# Revit family: RN 80022 Optipress-Aquaplus-Schiebemuffe
name_source: partatom
category: Rohrformteile
units: mm (PartAtom-declared; Revit-internal decimal feet)

## family parameters
Arbeitsebenenbasiert = Nein
Beim Laden mit Abzugskörper schneiden = Nein
Bemaßung runder Anschluss = Durchmesser verwenden
Gemeinsam genutzt = Nein
Immer vertikal = Ja
Teiletyp = Verbindung

## types (11) — shared parameters
1.010.00.2 Blattnummer der Richtlinie = 29
1.010.00.3 Ausgabedatum (Monat) der Richtlinie = 201308
1.010.00.4 Herstellername = R. Nussbaum AG
1.010.00.5 Revisionsdatum der Datei = 20190521
1.010.00.6 Webadresse des Herstellers = http://www.nussbaum.ch
1.100.00.4 Produktbezeichnung = Versorgung
1.110.00.2 Index = 4
1.110.00.4 Produktbezeichnung = Optipress
1.960/3L.00.8 Link (URL) = https://www.nussbaum.ch
29.700.00.4 Produktname = Optipress-Aquaplus-Schiebemuffe
29.700.00.5 Produktkennung = 2
29.700.00.6 Querschnittsform = 1
29.700.00.7 Nennweitensystem = DN
29.700.00.8 Nenndrucksystem = PN
29.710.02.4 Nenndruck = 16
29.710.02.5 max. zul. Überdruck [hPa] = 1600
29.710.02.7 max. zul. Dauer-Betriebsdruck [hPa] = 1600
29.710.02.9 max. zul. Dauer-Betriebstemperatur [°C] = 95
Connector Visibility = Nein
EnclosingSpace Visibility = Nein

## per-type parameters (varying)
- 80022.22, Optipress-Aquaplus-Schiebemuffe, DN=12, L=80: 1.800.00.3 TGA-Nummer=01900400000000000000000000000000000000000000000016000000000000000001; 1.810.00.3 Hersteller-Bestellnummer=80022.22; 1.810.00.4 DATANORM-Nummer=80022.22; 1.810.00.5 StLB-Nummer=265.212; 1.810.00.6 GTIN-Nummer=7612945051301; 29.710.02.10 Formstück-Gewicht [kg]=0.051; 29.710.02.3 Benennung=Optipress-Aquaplus-Schiebemuffe, DN=12, L=80; CONNECTOR0_DIAMETER_dX_0r=12 mm  [stored 0.0393701 ft]; CONNECTOR0_dX_01=22 mm; CONNECTOR0_ref_dX=22 mm; CONNECTOR1_DIAMETER_dX_0r=12 mm  [stored 0.0393701 ft]; CONNECTOR1_dX_00=59 mm; CONNECTOR1_dX_01=81 mm; CONNECTOR1_ref_dX=59 mm; R. Nussbaum AG 80022.22 de Visibility=Ja; R. Nussbaum AG 80022.23 de Visibility=Nein; R. Nussbaum AG 80022.24 de Visibility=Nein; R. Nussbaum AG 80022.25 de Visibility=Nein; R. Nussbaum AG 80022.26 de Visibility=Nein; R. Nussbaum AG 80022.27 de Visibility=Nein; R. Nussbaum AG 80022.28 de Visibility=Nein; R. Nussbaum AG 80022.70 de Visibility=Nein; R. Nussbaum AG 80022.71 de Visibility=Nein; R. Nussbaum AG 80022.72 de Visibility=Nein; R. Nussbaum AG 80022.73 de Visibility=Nein
- 80022.23, Optipress-Aquaplus-Schiebemuffe, DN=15, L=80: 1.800.00.3 TGA-Nummer=01900400000000000000000000000000000000000000000016000000000000000002; 1.810.00.3 Hersteller-Bestellnummer=80022.23; 1.810.00.4 DATANORM-Nummer=80022.23; 1.810.00.5 StLB-Nummer=265.213; 1.810.00.6 GTIN-Nummer=7612945051318; 29.710.02.10 Formstück-Gewicht [kg]=0.063; 29.710.02.3 Benennung=Optipress-Aquaplus-Schiebemuffe, DN=15, L=80; CONNECTOR0_DIAMETER_dX_0r=15 mm; CONNECTOR0_dX_01=22 mm; CONNECTOR0_ref_dX=22 mm; CONNECTOR1_DIAMETER_dX_0r=15 mm; CONNECTOR1_dX_00=59 mm; CONNECTOR1_dX_01=81 mm; CONNECTOR1_ref_dX=59 mm; R. Nussbaum AG 80022.22 de Visibility=Nein; R. Nussbaum AG 80022.23 de Visibility=Ja; R. Nussbaum AG 80022.24 de Visibility=Nein; R. Nussbaum AG 80022.25 de Visibility=Nein; R. Nussbaum AG 80022.26 de Visibility=Nein; R. Nussbaum AG 80022.27 de Visibility=Nein; R. Nussbaum AG 80022.28 de Visibility=Nein; R. Nussbaum AG 80022.70 de Visibility=Nein; R. Nussbaum AG 80022.71 de Visibility=Nein; R. Nussbaum AG 80022.72 de Visibility=Nein; R. Nussbaum AG 80022.73 de Visibility=Nein
- 80022.24, Optipress-Aquaplus-Schiebemuffe, DN=20, L=80: 1.800.00.3 TGA-Nummer=01900400000000000000000000000000000000000000000016000000000000000003; 1.810.00.3 Hersteller-Bestellnummer=80022.24; 1.810.00.4 DATANORM-Nummer=80022.24; 1.810.00.5 StLB-Nummer=265.214; 1.810.00.6 GTIN-Nummer=7612945051325; 29.710.02.10 Formstück-Gewicht [kg]=0.082; 29.710.02.3 Benennung=Optipress-Aquaplus-Schiebemuffe, DN=20, L=80; CONNECTOR0_DIAMETER_dX_0r=20 mm; CONNECTOR0_dX_01=24 mm; CONNECTOR0_ref_dX=24 mm; CONNECTOR1_DIAMETER_dX_0r=20 mm; CONNECTOR1_dX_00=57 mm; CONNECTOR1_dX_01=81 mm; CONNECTOR1_ref_dX=57 mm; R. Nussbaum AG 80022.22 de Visibility=Nein; R. Nussbaum AG 80022.23 de Visibility=Nein; R. Nussbaum AG 80022.24 de Visibility=Ja; R. Nussbaum AG 80022.25 de Visibility=Nein; R. Nussbaum AG 80022.26 de Visibility=Nein; R. Nussbaum AG 80022.27 de Visibility=Nein; R. Nussbaum AG 80022.28 de Visibility=Nein; R. Nussbaum AG 80022.70 de Visibility=Nein; R. Nussbaum AG 80022.71 de Visibility=Nein; R. Nussbaum AG 80022.72 de Visibility=Nein; R. Nussbaum AG 80022.73 de Visibility=Nein
- 80022.25, Optipress-Aquaplus-Schiebemuffe, DN=25, L=95: 1.800.00.3 TGA-Nummer=01900400000000000000000000000000000000000000000016000000000000000004; 1.810.00.3 Hersteller-Bestellnummer=80022.25; 1.810.00.4 DATANORM-Nummer=80022.25; 1.810.00.5 StLB-Nummer=265.215; 1.810.00.6 GTIN-Nummer=7612945051332; 29.710.02.10 Formstück-Gewicht [kg]=0.119; 29.710.02.3 Benennung=Optipress-Aquaplus-Schiebemuffe, DN=25, L=95; CONNECTOR0_DIAMETER_dX_0r=25 mm  [stored 0.082021 ft]; CONNECTOR0_dX_01=24 mm; CONNECTOR0_ref_dX=24 mm; CONNECTOR1_DIAMETER_dX_0r=25 mm  [stored 0.082021 ft]; CONNECTOR1_dX_00=72 mm; CONNECTOR1_dX_01=96 mm; CONNECTOR1_ref_dX=72 mm; R. Nussbaum AG 80022.22 de Visibility=Nein; R. Nussbaum AG 80022.23 de Visibility=Nein; R. Nussbaum AG 80022.24 de Visibility=Nein; R. Nussbaum AG 80022.25 de Visibility=Ja; R. Nussbaum AG 80022.26 de Visibility=Nein; R. Nussbaum AG 80022.27 de Visibility=Nein; R. Nussbaum AG 80022.28 de Visibility=Nein; R. Nussbaum AG 80022.70 de Visibility=Nein; R. Nussbaum AG 80022.71 de Visibility=Nein; R. Nussbaum AG 80022.72 de Visibility=Nein; R. Nussbaum AG 80022.73 de Visibility=Nein
- 80022.26, Optipress-Aquaplus-Schiebemuffe, DN=32, L=105: 1.800.00.3 TGA-Nummer=01900400000000000000000000000000000000000000000016000000000000000005; 1.810.00.3 Hersteller-Bestellnummer=80022.26; 1.810.00.4 DATANORM-Nummer=80022.26; 1.810.00.5 StLB-Nummer=265.216; 1.810.00.6 GTIN-Nummer=7612945051349; 29.710.02.10 Formstück-Gewicht [kg]=0.16; 29.710.02.3 Benennung=Optipress-Aquaplus-Schiebemuffe, DN=32, L=105; CONNECTOR0_DIAMETER_dX_0r=32 mm  [stored 0.104987 ft]; CONNECTOR0_dX_01=26 mm  [stored 0.0853018 ft]; CONNECTOR0_ref_dX=26 mm  [stored 0.0853018 ft]; CONNECTOR1_DIAMETER_dX_0r=32 mm  [stored 0.104987 ft]; CONNECTOR1_dX_00=80 mm; CONNECTOR1_dX_01=106 mm; CONNECTOR1_ref_dX=80 mm; R. Nussbaum AG 80022.22 de Visibility=Nein; R. Nussbaum AG 80022.23 de Visibility=Nein; R. Nussbaum AG 80022.24 de Visibility=Nein; R. Nussbaum AG 80022.25 de Visibility=Nein; R. Nussbaum AG 80022.26 de Visibility=Ja; R. Nussbaum AG 80022.27 de Visibility=Nein; R. Nussbaum AG 80022.28 de Visibility=Nein; R. Nussbaum AG 80022.70 de Visibility=Nein; R. Nussbaum AG 80022.71 de Visibility=Nein; R. Nussbaum AG 80022.72 de Visibility=Nein; R. Nussbaum AG 80022.73 de Visibility=Nein
- 80022.27, Optipress-Aquaplus-Schiebemuffe, DN=40, L=120: 1.800.00.3 TGA-Nummer=01900400000000000000000000000000000000000000000016000000000000000006; 1.810.00.3 Hersteller-Bestellnummer=80022.27; 1.810.00.4 DATANORM-Nummer=80022.27; 1.810.00.5 StLB-Nummer=265.217; 1.810.00.6 GTIN-Nummer=7612945051356; 29.710.02.10 Formstück-Gewicht [kg]=0.271; 29.710.02.3 Benennung=Optipress-Aquaplus-Schiebemuffe, DN=40, L=120; CONNECTOR0_DIAMETER_dX_0r=40 mm; CONNECTOR0_dX_01=36 mm; CONNECTOR0_ref_dX=36 mm; CONNECTOR1_DIAMETER_dX_0r=40 mm; CONNECTOR1_dX_00=85 mm; CONNECTOR1_dX_01=121 mm; CONNECTOR1_ref_dX=85 mm; R. Nussbaum AG 80022.22 de Visibility=Nein; R. Nussbaum AG 80022.23 de Visibility=Nein; R. Nussbaum AG 80022.24 de Visibility=Nein; R. Nussbaum AG 80022.25 de Visibility=Nein; R. Nussbaum AG 80022.26 de Visibility=Nein; R. Nussbaum AG 80022.27 de Visibility=Ja; R. Nussbaum AG 80022.28 de Visibility=Nein; R. Nussbaum AG 80022.70 de Visibility=Nein; R. Nussbaum AG 80022.71 de Visibility=Nein; R. Nussbaum AG 80022.72 de Visibility=Nein; R. Nussbaum AG 80022.73 de Visibility=Nein
- 80022.28, Optipress-Aquaplus-Schiebemuffe, DN=50, L=136: 1.800.00.3 TGA-Nummer=01900400000000000000000000000000000000000000000016000000000000000007; 1.810.00.3 Hersteller-Bestellnummer=80022.28; 1.810.00.4 DATANORM-Nummer=80022.28; 1.810.00.5 StLB-Nummer=265.218; 1.810.00.6 GTIN-Nummer=7612945051363; 29.710.02.10 Formstück-Gewicht [kg]=0.335; 29.710.02.3 Benennung=Optipress-Aquaplus-Schiebemuffe, DN=50, L=136; CONNECTOR0_DIAMETER_dX_0r=50 mm; CONNECTOR0_dX_01=40 mm; CONNECTOR0_ref_dX=40 mm; CONNECTOR1_DIAMETER_dX_0r=50 mm; CONNECTOR1_dX_00=96 mm; CONNECTOR1_dX_01=136 mm; CONNECTOR1_ref_dX=96 mm; R. Nussbaum AG 80022.22 de Visibility=Nein; R. Nussbaum AG 80022.23 de Visibility=Nein; R. Nussbaum AG 80022.24 de Visibility=Nein; R. Nussbaum AG 80022.25 de Visibility=Nein; R. Nussbaum AG 80022.26 de Visibility=Nein; R. Nussbaum AG 80022.27 de Visibility=Nein; R. Nussbaum AG 80022.28 de Visibility=Ja; R. Nussbaum AG 80022.70 de Visibility=Nein; R. Nussbaum AG 80022.71 de Visibility=Nein; R. Nussbaum AG 80022.72 de Visibility=Nein; R. Nussbaum AG 80022.73 de Visibility=Nein
- 80022.71, Optipress-Aquaplus-Schiebemuffe, DN=65, L=125: 1.800.00.3 TGA-Nummer=01900400000000000000000000000000000000000000000016000000000000000008; 1.810.00.3 Hersteller-Bestellnummer=80022.71; 1.810.00.4 DATANORM-Nummer=80022.71; 1.810.00.5 StLB-Nummer=265.221; 1.810.00.6 GTIN-Nummer=7612945655318; 29.710.02.10 Formstück-Gewicht [kg]=0.587; 29.710.02.3 Benennung=Optipress-Aquaplus-Schiebemuffe, DN=65, L=125; CONNECTOR0_DIAMETER_dX_0r=65 mm; CONNECTOR0_dX_01=50 mm; CONNECTOR0_ref_dX=50 mm; CONNECTOR1_DIAMETER_dX_0r=65 mm; CONNECTOR1_dX_00=75 mm; CONNECTOR1_dX_01=125 mm; CONNECTOR1_ref_dX=75 mm; R. Nussbaum AG 80022.22 de Visibility=Nein; R. Nussbaum AG 80022.23 de Visibility=Nein; R. Nussbaum AG 80022.24 de Visibility=Nein; R. Nussbaum AG 80022.25 de Visibility=Nein; R. Nussbaum AG 80022.26 de Visibility=Nein; R. Nussbaum AG 80022.27 de Visibility=Nein; R. Nussbaum AG 80022.28 de Visibility=Nein; R. Nussbaum AG 80022.70 de Visibility=Nein; R. Nussbaum AG 80022.71 de Visibility=Ja; R. Nussbaum AG 80022.72 de Visibility=Nein; R. Nussbaum AG 80022.73 de Visibility=Nein
- 80022.72, Optipress-Aquaplus-Schiebemuffe, DN=80, L=125: 1.800.00.3 TGA-Nummer=01900400000000000000000000000000000000000000000016000000000000000009; 1.810.00.3 Hersteller-Bestellnummer=80022.72; 1.810.00.4 DATANORM-Nummer=80022.72; 1.810.00.5 StLB-Nummer=265.222; 1.810.00.6 GTIN-Nummer=7612945655325; 29.710.02.10 Formstück-Gewicht [kg]=0.708; 29.710.02.3 Benennung=Optipress-Aquaplus-Schiebemuffe, DN=80, L=125; CONNECTOR0_DIAMETER_dX_0r=80 mm; CONNECTOR0_dX_01=50 mm; CONNECTOR0_ref_dX=50 mm; CONNECTOR1_DIAMETER_dX_0r=80 mm; CONNECTOR1_dX_00=75 mm; CONNECTOR1_dX_01=125 mm; CONNECTOR1_ref_dX=75 mm; R. Nussbaum AG 80022.22 de Visibility=Nein; R. Nussbaum AG 80022.23 de Visibility=Nein; R. Nussbaum AG 80022.24 de Visibility=Nein; R. Nussbaum AG 80022.25 de Visibility=Nein; R. Nussbaum AG 80022.26 de Visibility=Nein; R. Nussbaum AG 80022.27 de Visibility=Nein; R. Nussbaum AG 80022.28 de Visibility=Nein; R. Nussbaum AG 80022.70 de Visibility=Nein; R. Nussbaum AG 80022.71 de Visibility=Nein; R. Nussbaum AG 80022.72 de Visibility=Ja; R. Nussbaum AG 80022.73 de Visibility=Nein
- 80022.73, Optipress-Aquaplus-Schiebemuffe, DN=100, L=145: 1.800.00.3 TGA-Nummer=01900400000000000000000000000000000000000000000016000000000000000010; 1.810.00.3 Hersteller-Bestellnummer=80022.73; 1.810.00.4 DATANORM-Nummer=80022.73; 1.810.00.5 StLB-Nummer=265.223; 1.810.00.6 GTIN-Nummer=7612945655332; 29.710.02.10 Formstück-Gewicht [kg]=0.931; 29.710.02.3 Benennung=Optipress-Aquaplus-Schiebemuffe, DN=100, L=145; CONNECTOR0_DIAMETER_dX_0r=100 mm  [stored 0.328084 ft]; CONNECTOR0_dX_01=60 mm; CONNECTOR0_ref_dX=60 mm; CONNECTOR1_DIAMETER_dX_0r=100 mm  [stored 0.328084 ft]; CONNECTOR1_dX_00=85 mm; CONNECTOR1_dX_01=145 mm; CONNECTOR1_ref_dX=85 mm; R. Nussbaum AG 80022.22 de Visibility=Nein; R. Nussbaum AG 80022.23 de Visibility=Nein; R. Nussbaum AG 80022.24 de Visibility=Nein; R. Nussbaum AG 80022.25 de Visibility=Nein; R. Nussbaum AG 80022.26 de Visibility=Nein; R. Nussbaum AG 80022.27 de Visibility=Nein; R. Nussbaum AG 80022.28 de Visibility=Nein; R. Nussbaum AG 80022.70 de Visibility=Nein; R. Nussbaum AG 80022.71 de Visibility=Nein; R. Nussbaum AG 80022.72 de Visibility=Nein; R. Nussbaum AG 80022.73 de Visibility=Ja
- 80022.70, Optipress-Aquaplus-Schiebemuffe, DN=60, L=110: 1.800.00.3 TGA-Nummer=01900400000000000000000000000000000000000000000016000000000000000018; 1.810.00.3 Hersteller-Bestellnummer=80022.70; 1.810.00.4 DATANORM-Nummer=80022.70; 1.810.00.5 StLB-Nummer=265.224; 1.810.00.6 GTIN-Nummer=7612945667113; 29.710.02.10 Formstück-Gewicht [kg]=0.447; 29.710.02.3 Benennung=Optipress-Aquaplus-Schiebemuffe, DN=60, L=110; CONNECTOR0_DIAMETER_dX_0r=60 mm; CONNECTOR0_dX_01=43 mm  [stored 0.141076 ft]; CONNECTOR0_ref_dX=43 mm  [stored 0.141076 ft]; CONNECTOR1_DIAMETER_dX_0r=60 mm; CONNECTOR1_dX_00=67 mm; CONNECTOR1_dX_01=110 mm; CONNECTOR1_ref_dX=67 mm; R. Nussbaum AG 80022.22 de Visibility=Nein; R. Nussbaum AG 80022.23 de Visibility=Nein; R. Nussbaum AG 80022.24 de Visibility=Nein; R. Nussbaum AG 80022.25 de Visibility=Nein; R. Nussbaum AG 80022.26 de Visibility=Nein; R. Nussbaum AG 80022.27 de Visibility=Nein; R. Nussbaum AG 80022.28 de Visibility=Nein; R. Nussbaum AG 80022.70 de Visibility=Ja; R. Nussbaum AG 80022.71 de Visibility=Nein; R. Nussbaum AG 80022.72 de Visibility=Nein; R. Nussbaum AG 80022.73 de Visibility=Nein

note: column(s) folded — value = type name in every type: 1.800.00.4 Kommentarfeld

note: [stored X ft] marks values corroborated as IEEE doubles in the binary element streams (Revit-internal decimal feet)

## geometry (parser evidence)
native form markers: Sweep x2
no freeform markers — native parametric forms only
